# Revit family: Doppelhalter VS
name_source: partatom
category: HLS-Bauteile
revit_build: Autodesk Revit 2017 (Build: 20190507_1515(x64)
units: mm (PartAtom-declared; Revit-internal decimal feet)

## family parameters
Arbeitsebenenbasiert = Ja
Beim Laden mit Abzugskörper schneiden = Nein
Bemaßung runder Anschluss = Durchmesser verwenden
Gemeinsam genutzt = Ja
Immer vertikal = Nein
Raumberechnungspunkt = Nein
Teiletyp = Normal

## types (1)
- Doppelhalter VS, Gewindestift M 8x 30
    Achsabstand = 65 - 110 mm
    Artikelnummer = 0590199
    Breite = 23 mm  [stored 0.0754593 ft]
    EAN = 4250928415127
    Fabrikat = MEFA
    Firma = MEFA Befestigungs- und Montagesysteme GmbH
    Gewicht = 0.10 kg
    Gewicht pro Bauteil = 0.10 kg
    Gewindestifttyp = M8x30
    H = 30 mm  [stored 0.0984252 ft]
    Höhe = 30 mm
    Kurztext1 = Doppelhalter VS mit Gewindestift
    Kurztext2 = Achsabstand L 65 - 110 mm
    L = 110 mm
    Länge = 155 mm  [stored 0.50853 ft]
    Material = Stahl
    Mengeneinheit = St
    Vorgabe-Ansicht = 1219 mm
    max. zul. Last Zug = 0.15 kN
    vpe = 100 St

note: [stored X ft] marks values corroborated as IEEE doubles in the binary element streams (Revit-internal decimal feet)

## geometry (parser evidence)
native form markers: Sweep x1
no freeform markers — native parametric forms only
